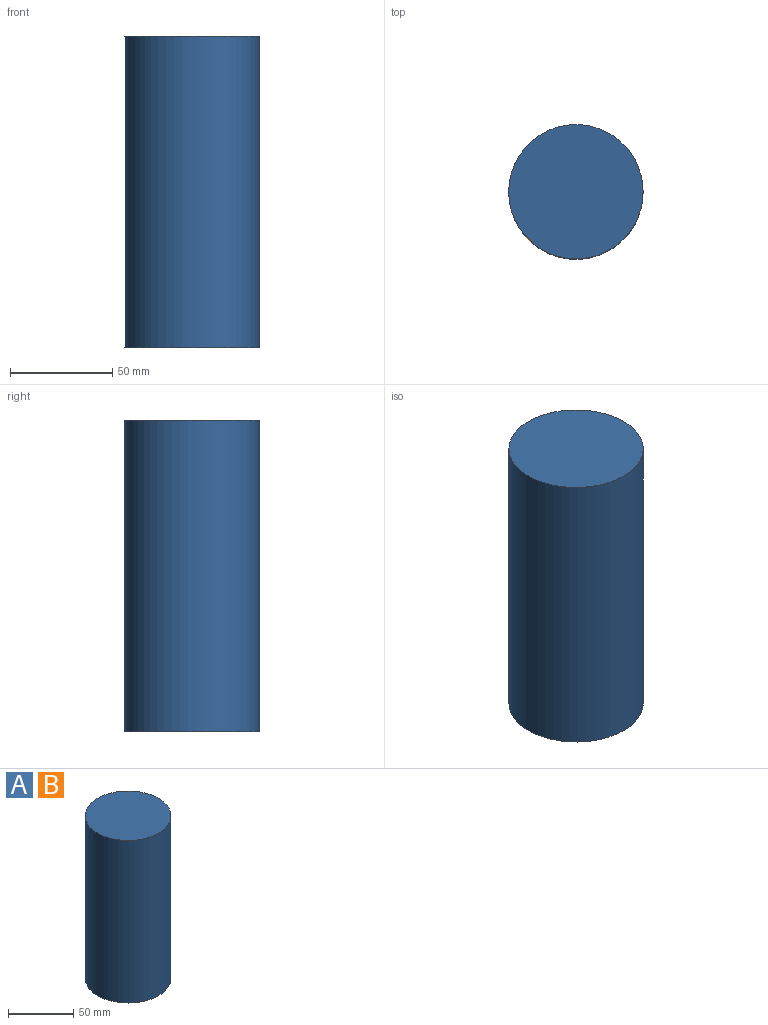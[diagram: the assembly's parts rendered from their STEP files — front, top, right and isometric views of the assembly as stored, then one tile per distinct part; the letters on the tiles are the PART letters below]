
ASSEMBLY  parts=2 mates=1
PART A: 3 faces, bbox 65.7x65.7x152.4 mm
  f0: cylinder r=32.83mm len=152.4mm, axis (0,0,-1), area 31433.6mm2, adj f1,f2
  f1: plane 65.65x65.65mm, normal (0,0,1), area 3385.4mm2, adj f0
  f2: plane 65.65x65.65mm, normal (0,0,-1), area 3385.4mm2, adj f0
PART B: same geometry as A
PLACE A at identity
PLACE B at identity
MATE cylindrical B.f0 <-> A.f0  axis (0,0,-1) through (0,0,0)mm
